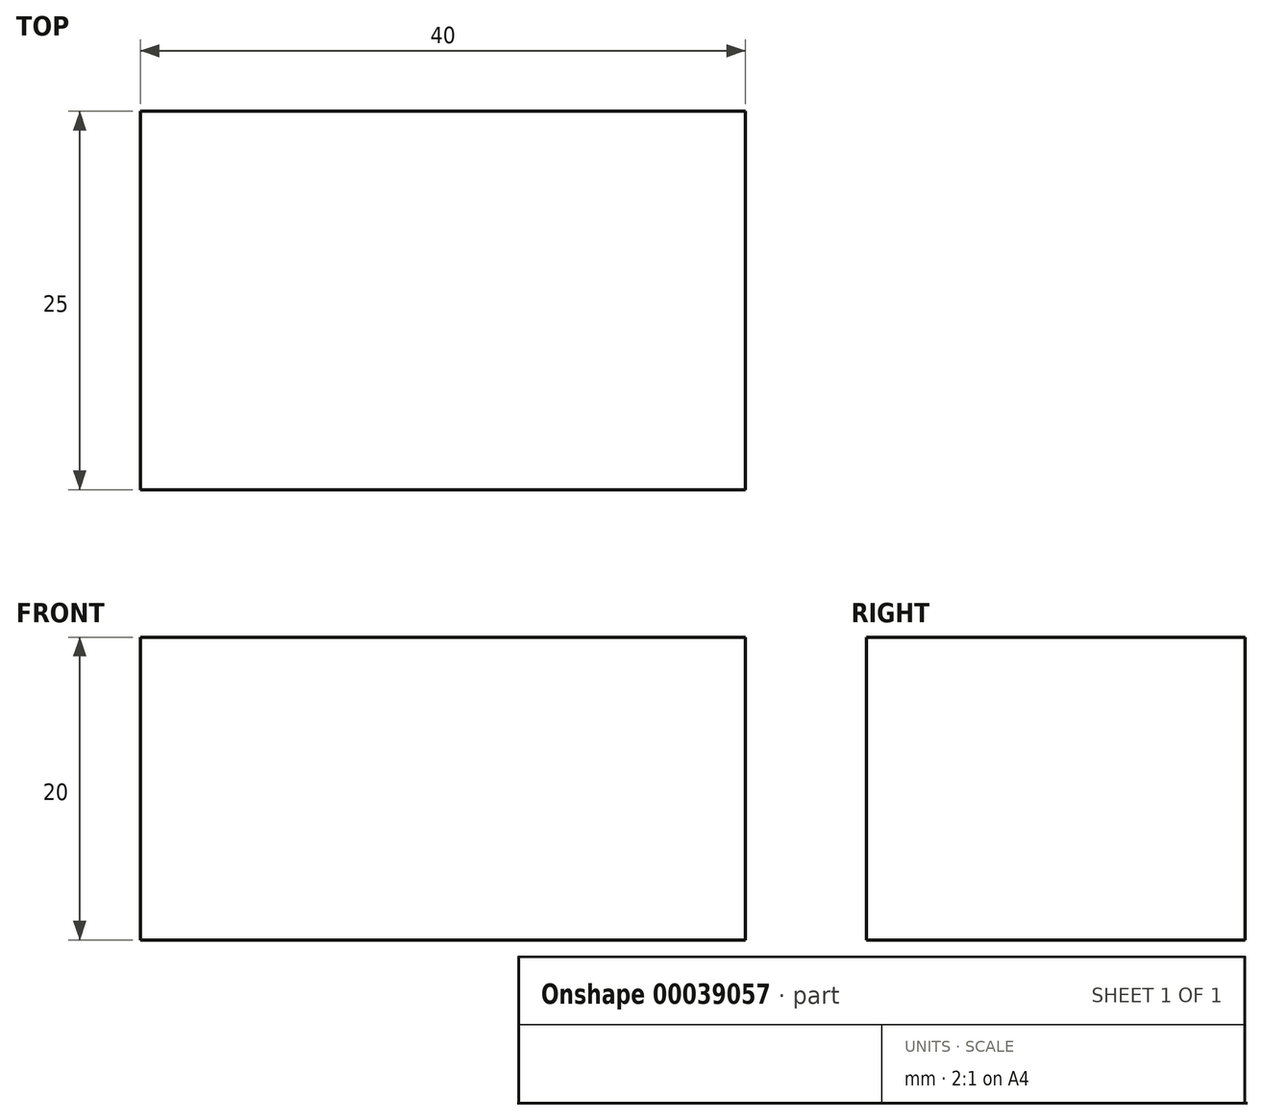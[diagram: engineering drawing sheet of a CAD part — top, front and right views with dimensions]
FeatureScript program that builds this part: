
annotation { "Feature Type Name" : "Feature", "Feature Type Description" : "" }
export const myFeature = defineFeature(function(context is Context, id is Id, definition is map)
    precondition{}
    {
        {
            var Q0;
            Q0=qCreatedBy(makeId("Front.planeOp"),FACE);
            var sketch = newSketch(context, id + "F0", { "sketchPlane" : qUnion([Q0])});
            skLineSegment(sketch, "E0.rect.bottom", {"start": v(20, 10) * mm, "end": v(-20, 10) * mm});
            skLineSegment(sketch, "E0.rect.top", {"start": v(20, -10) * mm, "end": v(-20, -10) * mm});
            skLineSegment(sketch, "E0.rect.left", {"start": v(20, 10) * mm, "end": v(20, -10) * mm});
            skLineSegment(sketch, "E0.rect.right", {"start": v(-20, 10) * mm, "end": v(-20, -10) * mm});
            skPoint(sketch, "E0.rect.middle", {"position": v(0, 0) * mm});
            skSolve(sketch);
        }
        {
            var Q0;
            Q0=makeQuery(id+"F0.imprint","IMPRINT",FACE,{"disambiguationData":[TD([[makeQuery(id+"F0.imprint","IMPRINT",EDGE,{"derivedFrom":sQuery(id+"F0.wireOp",EDGE,"E0.rect.bottom")}),1.0]])]});
            extrude(context, id + "F1", {"entities" : qUnion([Q0]), "depth" : 25 * mm});
        }
    });
